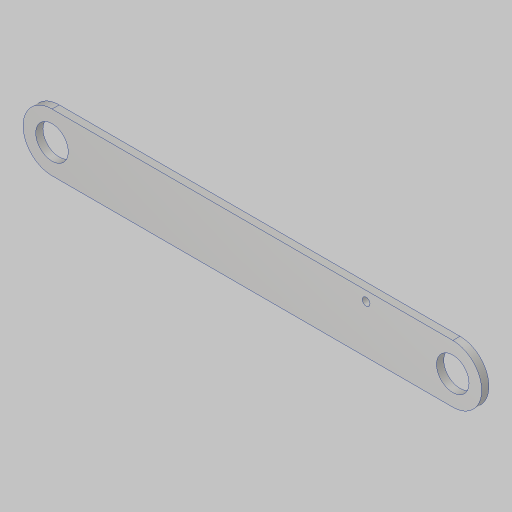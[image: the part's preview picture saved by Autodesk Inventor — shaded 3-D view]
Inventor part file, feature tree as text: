
AUTODESK INVENTOR PART (.ipt)
format: ipt  version: 2023.5 (Build 275446000, 446)  size: 108,544 bytes
history: native  units: in
note: dims shown in document units (in); Inventor stores cm internally (conversion verified against a paired STEP export)
features: sketch x2, extrude x1, hole x1
ambient origin geometry x8: Origin, YZ Plane, XZ Plane, XY Plane, X Axis, Y Axis, Z Axis, Center Point
bodies: Solid1 (feature_tree)
feature tree (4):
  extrude  "Extrusion1"  Depth=13.873in
  hole  "Hole1"  [1 undecoded]
  sketch  "Sketch1"  dims[d0=1.125in d1=13.873in]
  sketch  "Sketch2"  dims[d2=2.0in d3=0.25in d4=0.0in d6=0.266in d7=0.5in d8=0.507in d9=0.25in d10=0.5635in d11=0.75in d12=0.8108in d14=10.875in d15=0.663in]
note: 1 required parameter value undecoded (feature->parameter linkage not recoverable at this tier; creation-order binding heuristic only, values carry confidence <= 0.55)
